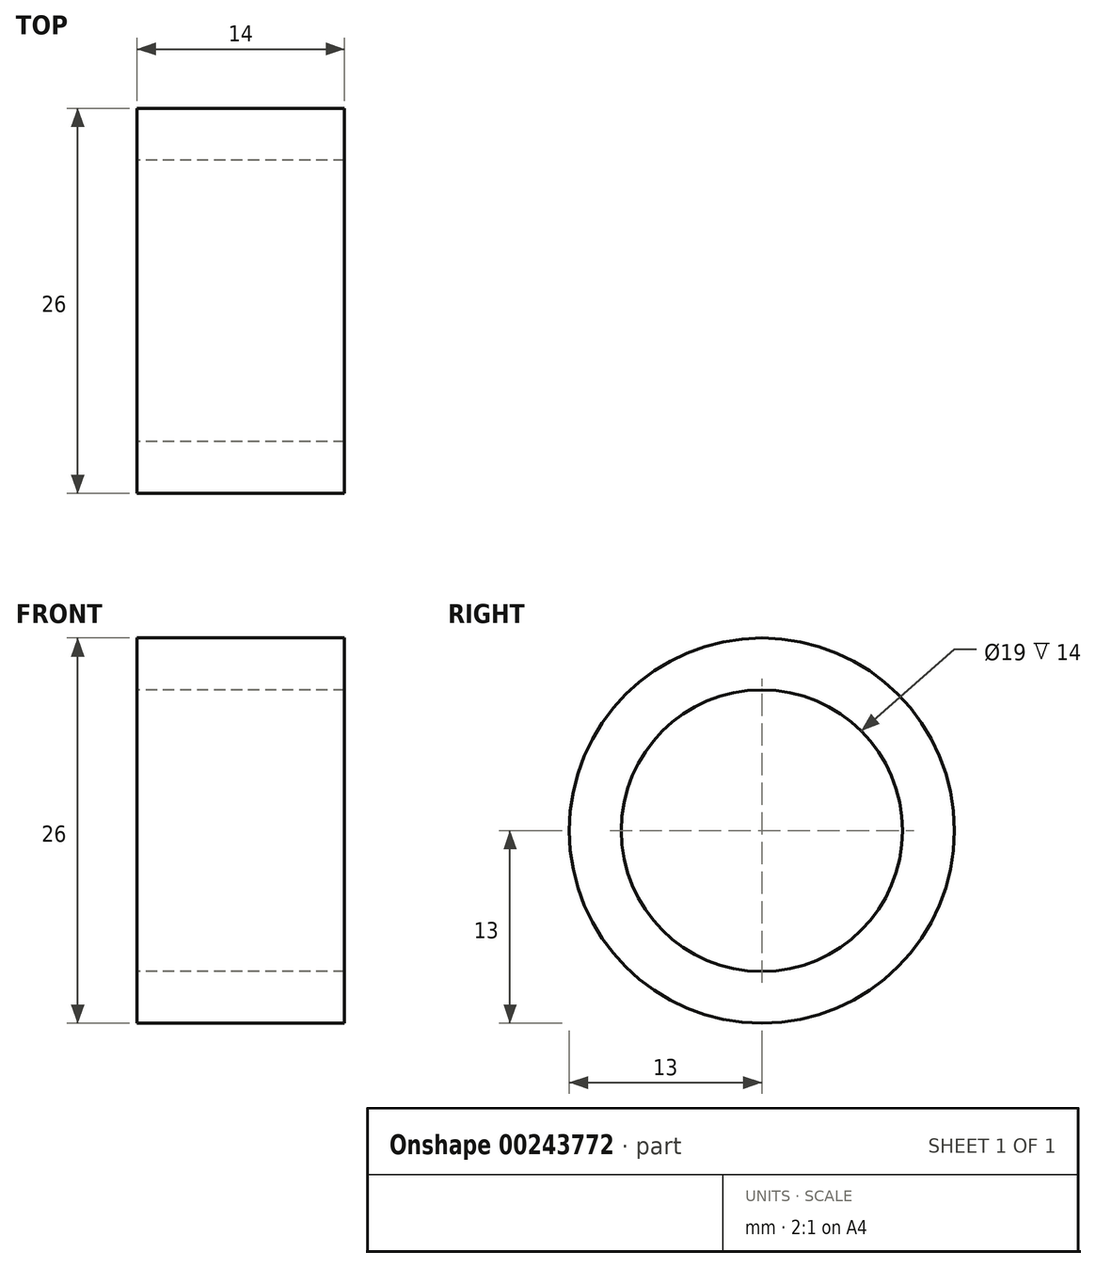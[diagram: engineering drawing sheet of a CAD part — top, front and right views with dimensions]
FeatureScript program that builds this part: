
annotation { "Feature Type Name" : "Feature", "Feature Type Description" : "" }
export const myFeature = defineFeature(function(context is Context, id is Id, definition is map)
    precondition{}
    {
        {
            var Q0;
            Q0=qCreatedBy(makeId("Front.planeOp"),FACE);
            var sketch = newSketch(context, id + "F0", { "sketchPlane" : qUnion([Q0])});
            skLineSegment(sketch, "E0.bottom", {"start": v(0, 13) * mm, "end": v(14, 13) * mm});
            skLineSegment(sketch, "E0.top", {"start": v(0, 9.5) * mm, "end": v(14, 9.5) * mm});
            skLineSegment(sketch, "E0.left", {"start": v(0, 13) * mm, "end": v(0, 9.5) * mm});
            skLineSegment(sketch, "E0.right", {"start": v(14, 13) * mm, "end": v(14, 9.5) * mm});
            skLineSegment(sketch, "E1", {"start": v(-3.5, 0) * mm, "end": v(15.92, 0) * mm, "construction": true});
            skSolve(sketch);
        }
        {
            var Q0;
            Q0=makeQuery(id+"F0.imprint","IMPRINT",FACE,{"disambiguationData":[TD([[makeQuery(id+"F0.imprint","IMPRINT",EDGE,{"derivedFrom":sQuery(id+"F0.wireOp",EDGE,"E0.bottom")}),-1.0]])]});
            var Q1;
            Q1=sQuery(id+"F0.wireOp",EDGE,"E1");
            revolve(context, id + "F1", {"entities" : qUnion([Q0]), "axis" : qUnion([Q1]), "revolveType" : RevolveType.FULL});
        }
    });
